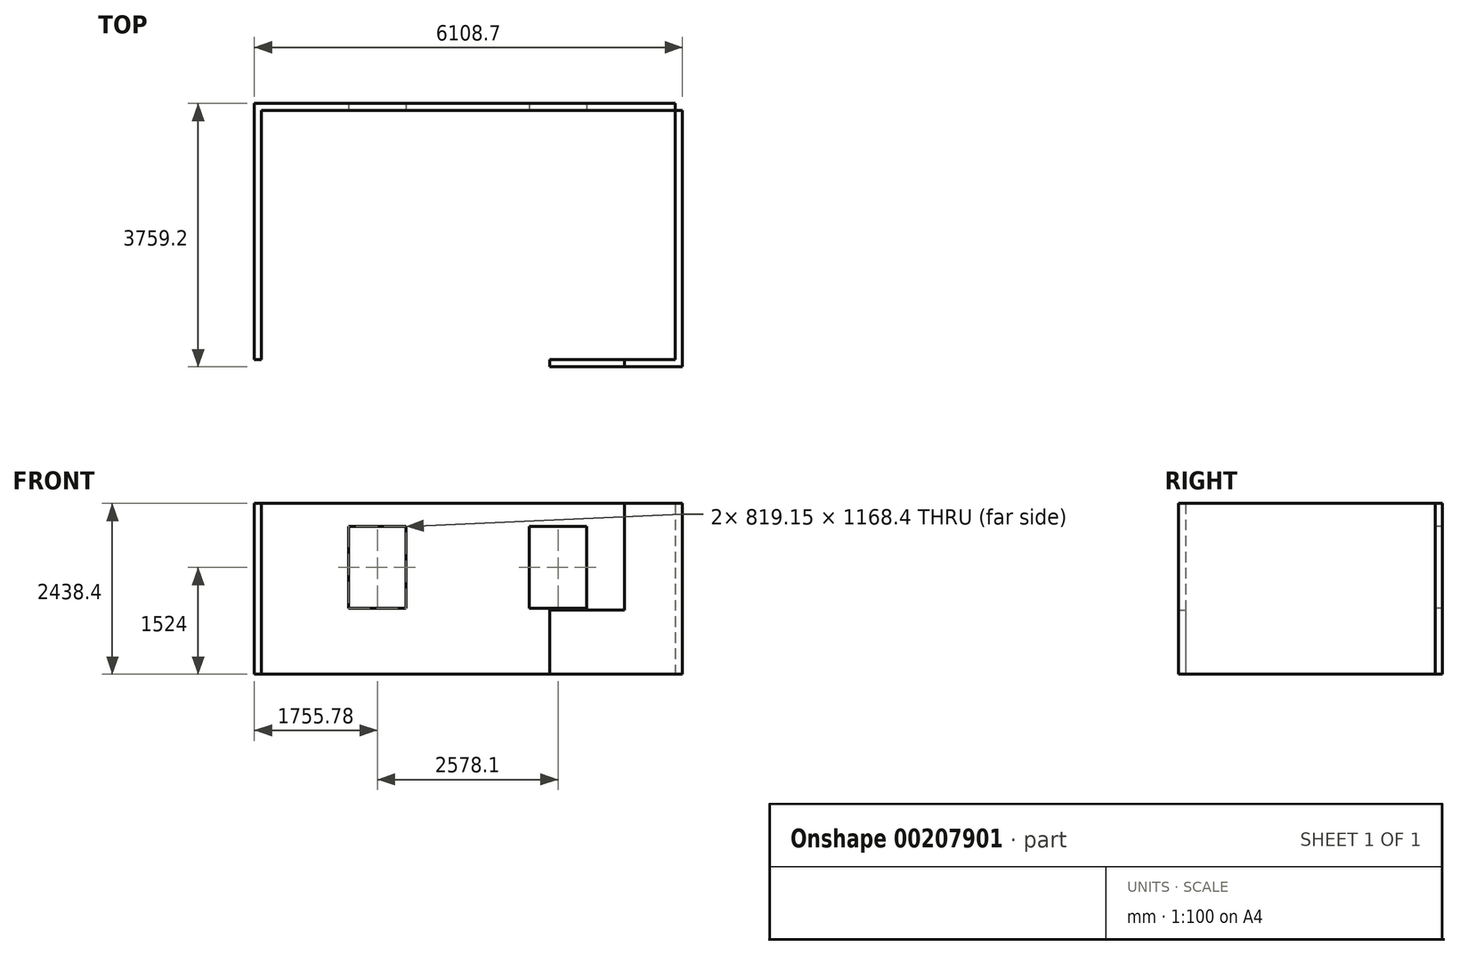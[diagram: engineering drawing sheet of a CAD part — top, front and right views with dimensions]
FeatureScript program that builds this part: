
annotation { "Feature Type Name" : "Feature", "Feature Type Description" : "" }
export const myFeature = defineFeature(function(context is Context, id is Id, definition is map)
    precondition{}
    {
        {
            var Q0;
            Q0=qCreatedBy(makeId("Top.planeOp"),FACE);
            var sketch = newSketch(context, id + "F0", { "sketchPlane" : qUnion([Q0])});
            skLineSegment(sketch, "E0.bottom", {"start": v(0, 0) * mm, "end": v(101.6, 0) * mm});
            skLineSegment(sketch, "E0.top", {"start": v(0, -3556) * mm, "end": v(101.6, -3556) * mm});
            skLineSegment(sketch, "E0.left", {"start": v(0, 0) * mm, "end": v(0, -3556) * mm});
            skLineSegment(sketch, "E0.right", {"start": v(101.6, 0) * mm, "end": v(101.6, -3556) * mm});
            skLineSegment(sketch, "E1.bottom", {"start": v(0, 0) * mm, "end": v(-5905.5, 0) * mm});
            skLineSegment(sketch, "E1.top", {"start": v(0, 101.6) * mm, "end": v(-5905.5, 101.6) * mm});
            skLineSegment(sketch, "E1.left", {"start": v(0, 0) * mm, "end": v(0, 101.6) * mm});
            skLineSegment(sketch, "E1.right", {"start": v(-5905.5, 0) * mm, "end": v(-5905.5, 101.6) * mm});
            skLineSegment(sketch, "E2.bottom", {"start": v(0, -3556) * mm, "end": v(-723.9, -3556) * mm});
            skLineSegment(sketch, "E2.top", {"start": v(0, -3657.6) * mm, "end": v(-723.9, -3657.6) * mm});
            skLineSegment(sketch, "E2.left", {"start": v(0, -3556) * mm, "end": v(0, -3657.6) * mm});
            skLineSegment(sketch, "E2.right", {"start": v(-723.9, -3556) * mm, "end": v(-723.9, -3657.6) * mm});
            skLineSegment(sketch, "E3.bottom", {"start": v(-5905.5, 101.6) * mm, "end": v(-6007.1, 101.6) * mm});
            skLineSegment(sketch, "E3.top", {"start": v(-5905.5, -3556) * mm, "end": v(-6007.1, -3556) * mm});
            skLineSegment(sketch, "E3.left", {"start": v(-5905.5, 101.6) * mm, "end": v(-5905.5, -3556) * mm});
            skLineSegment(sketch, "E3.right", {"start": v(-6007.1, 101.6) * mm, "end": v(-6007.1, -3556) * mm});
            skLineSegment(sketch, "E4.top", {"start": v(0, -3657.6) * mm, "end": v(101.6, -3657.6) * mm});
            skLineSegment(sketch, "E4.right", {"start": v(101.6, -3556) * mm, "end": v(101.6, -3657.6) * mm});
            skLineSegment(sketch, "E5.bottom", {"start": v(101.6, 0) * mm, "end": v(0, 0) * mm});
            skLineSegment(sketch, "E5.top", {"start": v(101.6, 101.6) * mm, "end": v(0, 101.6) * mm});
            skLineSegment(sketch, "E5.left", {"start": v(101.6, 0) * mm, "end": v(101.6, 101.6) * mm});
            skPoint(sketch, "E6.right.end.orphan", {"position": v(-1837.78, -3657.6) * mm});
            skSolve(sketch);
        }
        {
            var Q0;
            Q0=makeQuery(id+"F0.imprint","IMPRINT",FACE,{"disambiguationData":[TD([[makeQuery(id+"F0.imprint","IMPRINT",EDGE,{"derivedFrom":sQuery(id+"F0.wireOp",EDGE,"E2.bottom")}),1.0]])]});
            var Q1;
            Q1=makeQuery(id+"F0.imprint","IMPRINT",FACE,{"disambiguationData":[TD([[makeQuery(id+"F0.imprint","IMPRINT",EDGE,{"derivedFrom":sQuery(id+"F0.wireOp",EDGE,"E0.top")}),-1.0]])]});
            var Q2;
            Q2=makeQuery(id+"F0.imprint","IMPRINT",FACE,{"disambiguationData":[TD([[makeQuery(id+"F0.imprint","IMPRINT",EDGE,{"derivedFrom":sQuery(id+"F0.wireOp",EDGE,"E0.left")}),1.0]])]});
            var Q3;
            Q3=makeQuery(id+"F0.imprint","IMPRINT",FACE,{"disambiguationData":[TD([[makeQuery(id+"F0.imprint","IMPRINT",EDGE,{"derivedFrom":sQuery(id+"F0.wireOp",EDGE,"E5.bottom")}),-1.0]])]});
            var Q4;
            {var subQ0=sQuery(id+"F0.wireOp",EDGE,"E1.bottom");Q4=makeQuery(id+"F0.imprint","IMPRINT",FACE,{"disambiguationData":[TD([[makeQuery(id+"F0.imprint","IMPRINT",EDGE,{"derivedFrom":subQ0}),-1.0]])]});}
            var Q5;
            {var subQ3=sQuery(id+"F0.wireOp",EDGE,"E3.bottom");Q5=makeQuery(id+"F0.imprint","IMPRINT",FACE,{"disambiguationData":[TD([[makeQuery(id+"F0.imprint","IMPRINT",EDGE,{"derivedFrom":subQ3}),1.0]])]});}
            extrude(context, id + "F1", {"entities" : qUnion([Q0, Q1, Q2, Q3, Q4, Q5]), "depth" : 2438.4 * mm});
        }
        {
            var Q0;
            Q0=qCreatedBy(makeId("Top.planeOp"),FACE);
            var sketch = newSketch(context, id + "F2", { "sketchPlane" : qUnion([Q0])});
            skLineSegment(sketch, "E7.bottom", {"start": v(-723.9, -3657.6) * mm, "end": v(-1790.7, -3657.6) * mm});
            skLineSegment(sketch, "E7.top", {"start": v(-723.9, -3556) * mm, "end": v(-1790.7, -3556) * mm});
            skLineSegment(sketch, "E7.left", {"start": v(-723.9, -3657.6) * mm, "end": v(-723.9, -3556) * mm});
            skLineSegment(sketch, "E7.right", {"start": v(-1790.7, -3657.6) * mm, "end": v(-1790.7, -3556) * mm});
            skSolve(sketch);
        }
        {
            var Q0;
            Q0=makeQuery(id+"F2.imprint","IMPRINT",FACE,{"disambiguationData":[TD([[makeQuery(id+"F2.imprint","IMPRINT",EDGE,{"derivedFrom":sQuery(id+"F2.wireOp",EDGE,"E7.bottom")}),-1.0]])]});
            extrude(context, id + "F3", {"entities" : qUnion([Q0]), "operationType" : NewBodyOperationType.ADD, "depth" : 914.4 * mm});
        }
        {
            var Q0;
            Q0=makeQuery(id+"F1.opExtrude","SWEPT_FACE",FACE,{"disambiguationData":[OSD([sQuery(id+"F0.wireOp",EDGE,"E1.bottom")])]});
            var sketch = newSketch(context, id + "F4", { "sketchPlane" : qUnion([Q0])});
            skLineSegment(sketch, "E8.bottom", {"start": v(-1263.65, 2108.2) * mm, "end": v(-2082.8, 2108.2) * mm});
            skLineSegment(sketch, "E8.top", {"start": v(-1263.65, 939.8) * mm, "end": v(-2082.8, 939.8) * mm});
            skLineSegment(sketch, "E8.left", {"start": v(-1263.65, 2108.2) * mm, "end": v(-1263.65, 939.8) * mm});
            skLineSegment(sketch, "E8.right", {"start": v(-2082.8, 2108.2) * mm, "end": v(-2082.8, 939.8) * mm});
            skLineSegment(sketch, "E9.bottom", {"start": v(-4660.9, 2108.2) * mm, "end": v(-3841.75, 2108.2) * mm});
            skLineSegment(sketch, "E9.top", {"start": v(-4660.9, 939.8) * mm, "end": v(-3841.75, 939.8) * mm});
            skLineSegment(sketch, "E9.left", {"start": v(-4660.9, 2108.2) * mm, "end": v(-4660.9, 939.8) * mm});
            skLineSegment(sketch, "E9.right", {"start": v(-3841.75, 2108.2) * mm, "end": v(-3841.75, 939.8) * mm});
            skSolve(sketch);
        }
        {
            var Q0;
            Q0 = qSketchRegion(id + "F4", true);
            extrude(context, id + "F5", {"entities" : qUnion([Q0]), "operationType" : NewBodyOperationType.REMOVE, "endBound" : BoundingType.UP_TO_NEXT, "oppositeDirection" : true, "depth" : 101.6 * mm});
        }
    });
